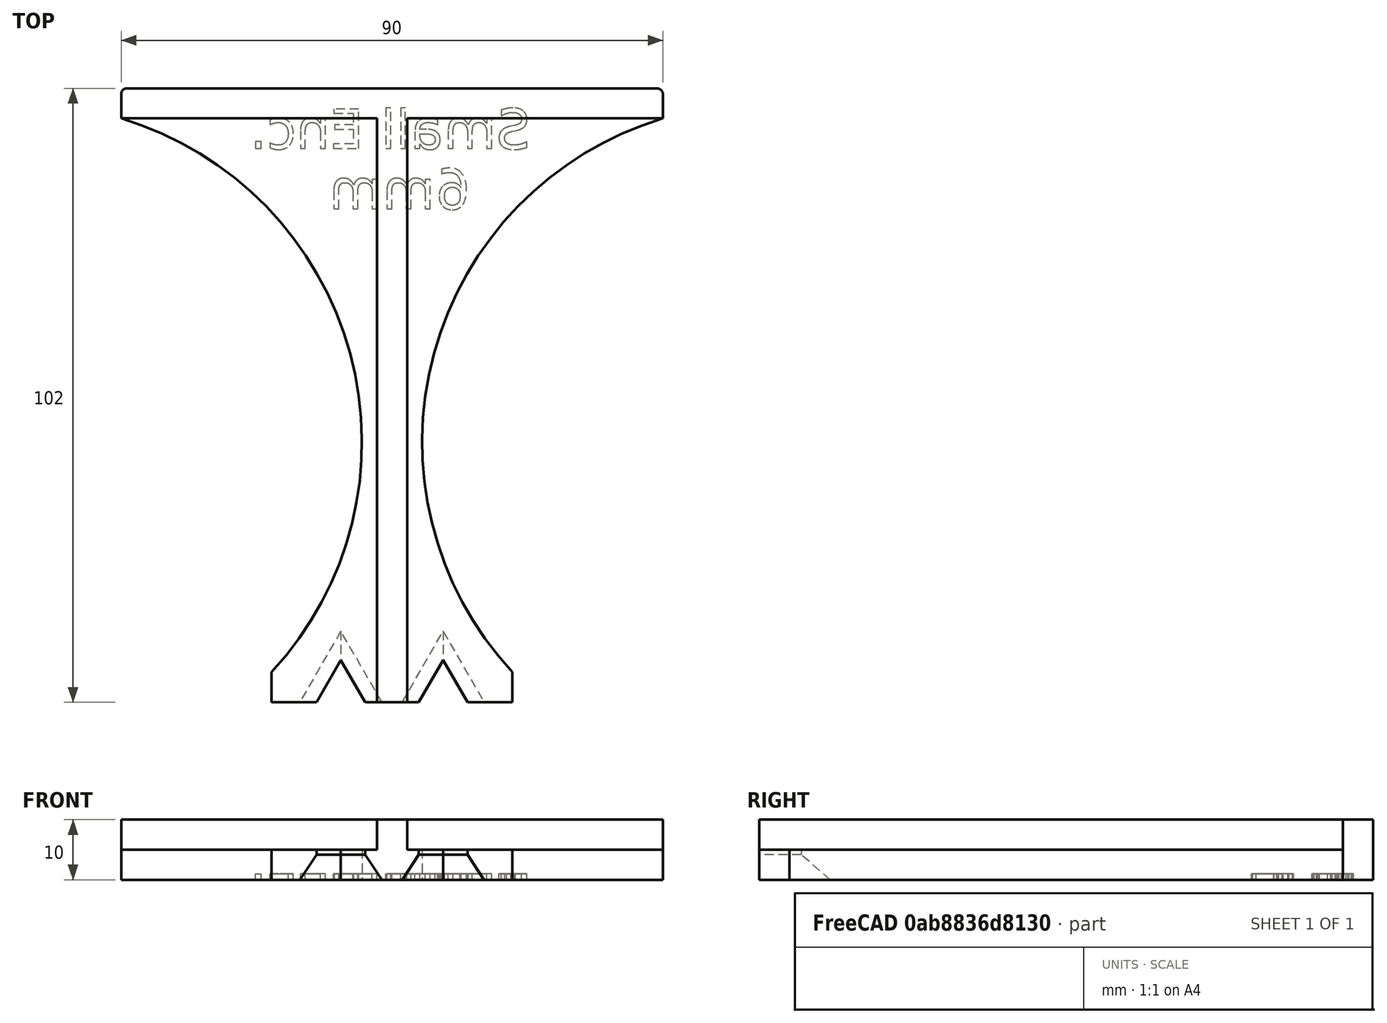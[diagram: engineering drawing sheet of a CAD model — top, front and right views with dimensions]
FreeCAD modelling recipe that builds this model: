
FCSTD DOCUMENT  (FreeCAD 0.19R24276 (Git))
Label: Small enclosure, 6mm DIN holes
License: All rights reserved
LicenseURL: http://en.wikipedia.org/wiki/All_rights_reserved
objects: PartDesign::Pocket×4, Sketcher::SketchObject×3, Part::Part2DObjectPython×2, PartDesign::Pad×1, PartDesign::Chamfer×1, PartDesign::Fillet×1, PartDesign::Body×1
note: 20 computed .brp shape members not serialized (recipe doc carries the construction recipe); baked Part::Feature solids carry a one-line shape summary decoded from their .brp

FEATURE [Sketcher::SketchObject] Sketch
  FullyConstrained = true
  MapMode = 5
  Support = -> [XY_Plane]
  sketch-geometry (11):
    g0: LineSegment StartX=-45 StartY=0 StartZ=0 EndX=45 EndY=0 EndZ=0
    g1: LineSegment StartX=-20 StartY=-102 StartZ=0 EndX=20 EndY=-102 EndZ=0
    g2: ArcOfCircle CenterX=61.167 CenterY=-58.7899 CenterZ=0 NormalX=0 NormalY=0 NormalZ=1 AngleXU=0 Radius=56.167 StartAngle=1.86276 EndAngle=3.88976
    g3: GeomPoint X=0 Y=-102 Z=0
    g4: ArcOfCircle CenterX=-61.167 CenterY=-58.7899 CenterZ=0 NormalX=0 NormalY=0 NormalZ=1 AngleXU=0 Radius=56.167 StartAngle=5.53502 EndAngle=7.56201
    g5: LineSegment StartX=45 StartY=0 StartZ=0 EndX=45 EndY=-5 EndZ=0
    g6: LineSegment StartX=-45 StartY=0 StartZ=0 EndX=-45 EndY=-5 EndZ=0
    g7: GeomPoint X=5 Y=-58.7899 Z=0
    g8: LineSegment StartX=-61.167 StartY=-58.7899 StartZ=0 EndX=61.167 EndY=-58.7899 EndZ=0
    g9: LineSegment StartX=20 StartY=-97 StartZ=0 EndX=20 EndY=-102 EndZ=0
    g10: LineSegment StartX=-20 StartY=-97 StartZ=0 EndX=-20 EndY=-102 EndZ=0
  constraints (30):
    c: Horizontal(g0)
    c: Horizontal(g1)
    c: Distance(g0) = 90
    c: Symmetric(g0,g0,g-1)
    c: DistanceY(g1,g-1) = 102
    c: Symmetric(g1,g1,g3)
    c: Vertical(g-1,g3)
    c: Distance(g1) = 40
    c: Horizontal(g4,g2)
    c: Coincident(g5,g0)
    c: Coincident(g5,g2)
    c: Coincident(g6,g0)
    c: Coincident(g6,g4)
    c: Vertical(g5)
    c: Vertical(g6)
    c: DistanceY(g5,g5) = 5
    c: Equal(g5,g6)
    c: PointOnObject(g7,g2)
    c: DistanceX(g-1,g7) = 5
    c: Coincident(g8,g4)
    c: Coincident(g8,g2)
    c: PointOnObject(g7,g8)
    c: Coincident(g9,g2)
    c: Coincident(g9,g1)
    c: Coincident(g10,g4)
    c: Coincident(g10,g1)
    c: Vertical(g9)
    c: Vertical(g10)
    c: Distance(g9) = 5
    c: Equal(g9,g10)
FEATURE [PartDesign::Pad] Pad
  Direction = (1,1,1)
  Length = 10
  Length2 = 100
  Midplane = true
  Profile = -> Sketch
  Type = 0
FEATURE [Sketcher::SketchObject] Sketch001
  FullyConstrained = true
  MapMode = 5
  Support = -> [XY_Plane]
  sketch-geometry (8):
    g0: LineSegment StartX=-52.5 StartY=-5 StartZ=0 EndX=-2.5 EndY=-5 EndZ=0
    g1: LineSegment StartX=-2.5 StartY=-5 StartZ=0 EndX=-2.5 EndY=-155 EndZ=0
    g2: LineSegment StartX=-2.5 StartY=-155 StartZ=0 EndX=-52.5 EndY=-155 EndZ=0
    g3: LineSegment StartX=-52.5 StartY=-155 StartZ=0 EndX=-52.5 EndY=-5 EndZ=0
    g4: LineSegment StartX=2.5 StartY=-5 StartZ=0 EndX=52.5 EndY=-5 EndZ=0
    g5: LineSegment StartX=52.5 StartY=-5 StartZ=0 EndX=52.5 EndY=-155 EndZ=0
    g6: LineSegment StartX=52.5 StartY=-155 StartZ=0 EndX=2.5 EndY=-155 EndZ=0
    g7: LineSegment StartX=2.5 StartY=-155 StartZ=0 EndX=2.5 EndY=-5 EndZ=0
  constraints (23):
    c: Coincident(g0,g1)
    c: Coincident(g1,g2)
    c: Coincident(g2,g3)
    c: Coincident(g3,g0)
    c: Horizontal(g0)
    c: Horizontal(g2)
    c: Vertical(g1)
    c: Vertical(g3)
    c: Coincident(g4,g5)
    c: Coincident(g5,g6)
    c: Coincident(g6,g7)
    c: Coincident(g7,g4)
    c: Horizontal(g4)
    c: Horizontal(g6)
    c: Vertical(g5)
    c: Vertical(g7)
    c: Horizontal(g1,g6)
    c: Equal(g0,g4)
    c: DistanceY(g4,g-1) = 5
    c: Distance(g5) = 150
    c: DistanceX(g0,g4) = 5
    c: Symmetric(g4,g0,g-2)
    c: DistanceX(g6,g6) = 50
FEATURE [PartDesign::Pocket] Pocket
  BaseFeature = -> Pad
  Length = 5
  Length2 = 100
  Profile = -> Sketch001
  Reversed = true
  Type = 0
FEATURE [Sketcher::SketchObject] Sketch002
  ExternalGeometry = -> [Pocket]
  FullyConstrained = true
  MapMode = 5
  Support = -> [XY_Plane]
  sketch-geometry (6):
    g0: LineSegment StartX=8.5 StartY=-95 StartZ=0 EndX=3.5 EndY=-103.66 EndZ=0
    g1: LineSegment StartX=3.5 StartY=-103.66 StartZ=0 EndX=13.5 EndY=-103.66 EndZ=0
    g2: LineSegment StartX=13.5 StartY=-103.66 StartZ=0 EndX=8.5 EndY=-95 EndZ=0
    g3: LineSegment StartX=-8.5 StartY=-95 StartZ=0 EndX=-3.5 EndY=-103.66 EndZ=0
    g4: LineSegment StartX=-3.5 StartY=-103.66 StartZ=0 EndX=-13.5 EndY=-103.66 EndZ=0
    g5: LineSegment StartX=-13.5 StartY=-103.66 StartZ=0 EndX=-8.5 EndY=-95 EndZ=0
  constraints (18):
    c: Coincident(g0,g1)
    c: Horizontal(g1)
    c: Coincident(g1,g2)
    c: Coincident(g2,g0)
    c: Equal(g0,g2)
    c: Equal(g2,g1)
    c: DistanceY(g0,g-3) = 90
    c: Distance(g1) = 10
    c: Coincident(g3,g4)
    c: Horizontal(g4)
    c: Coincident(g4,g5)
    c: Coincident(g5,g3)
    c: Equal(g0,g3)
    c: Equal(g3,g5)
    c: Equal(g5,g4)
    c: Horizontal(g0,g3)
    c: DistanceX(g3,g-4) = 6
    c: DistanceX(g-5,g0) = 6
FEATURE [PartDesign::Pocket] Pocket001
  BaseFeature = -> Pocket
  Length = 5
  Length2 = 100
  Profile = -> Sketch002
  Type = 1
FEATURE [PartDesign::Chamfer] Chamfer
  Angle = 60
  Base = -> Pocket001 [Edge16,Edge17,Edge19,Edge20]
  BaseFeature = -> Pocket001
  ChamferType = 2
  FlipDirection = false
  Size = 2.4
  Size2 = 1
  SupportTransform = false
FEATURE [Part::Part2DObjectPython] ShapeString  # Draft 2D object (typed FeaturePython)
  FontFile = <path>
  Placement = pos=(23,-10,-5) rot=(0,1,0;3.14159rad)
  Size = 7
  String = Small Enc.
  Tracking = 0
FEATURE [Part::Part2DObjectPython] ShapeString001  # Draft 2D object (typed FeaturePython)
  FontFile = <path>
  Placement = pos=(13,-20,-5) rot=(0,1,0;3.14159rad)
  Size = 7
  String = 6mm
  Tracking = 0
FEATURE [PartDesign::Pocket] Pocket002
  BaseFeature = -> Chamfer
  Length = 1
  Length2 = 100
  Profile = -> ShapeString
  Type = 0
FEATURE [PartDesign::Pocket] Pocket003
  BaseFeature = -> Pocket002
  Length = 1
  Length2 = 100
  Profile = -> ShapeString001
  Type = 0
FEATURE [PartDesign::Fillet] Fillet
  Base = -> Pocket003 [Edge239,Edge244,Edge238]
  BaseFeature = -> Pocket003
  Radius = 3
  SupportTransform = false
FEATURE [PartDesign::Body] Body
  Group = -> [Sketch,Pad,Sketch001,Pocket,Sketch002,Pocket001,Chamfer,ShapeString,Pocket002,ShapeString001,Pocket003,Fillet]
  Origin = -> Origin
  Tip = -> Fillet
note: 2 file-system paths scrubbed to <path> (originals preserved in the JSON sidecar)
